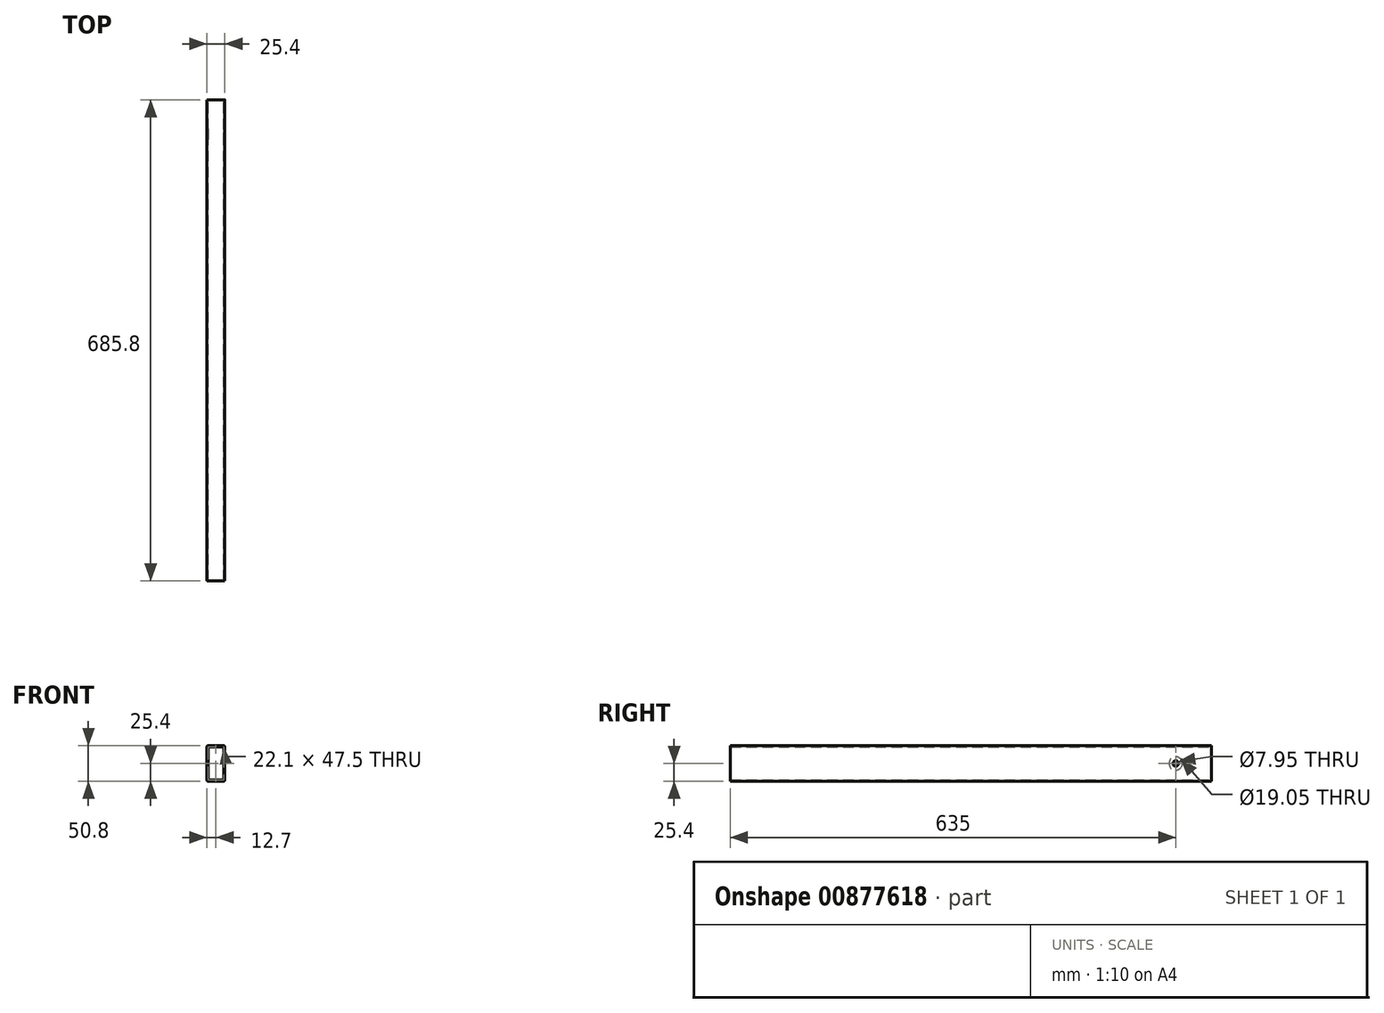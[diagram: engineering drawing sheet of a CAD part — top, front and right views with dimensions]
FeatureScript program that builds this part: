
annotation { "Feature Type Name" : "Feature", "Feature Type Description" : "" }
export const myFeature = defineFeature(function(context is Context, id is Id, definition is map)
    precondition{}
    {
        {
            var Q0;
            Q0=qCreatedBy(makeId("Front.planeOp"),FACE);
            var sketch = newSketch(context, id + "F0", { "sketchPlane" : qUnion([Q0])});
            skLineSegment(sketch, "E0.bottom", {"start": v(1.65, 0) * mm, "end": v(23.75, 0) * mm});
            skLineSegment(sketch, "E0.top", {"start": v(1.65, 50.8) * mm, "end": v(23.75, 50.8) * mm});
            skLineSegment(sketch, "E0.left", {"start": v(0, 1.65) * mm, "end": v(0, 49.15) * mm});
            skLineSegment(sketch, "E0.right", {"start": v(25.4, 1.65) * mm, "end": v(25.4, 49.15) * mm});
            skPoint(sketch, "E1.visualSharp", {"position": v(0, 50.8) * mm});
            skArc(sketch, "E1.filletArc", {"start": v(1.65, 50.8) * mm, "mid": v(0.48, 50.32) * mm, "end": v(0, 49.15) * mm});
            skPoint(sketch, "E2.visualSharp", {"position": v(25.4, 50.8) * mm});
            skArc(sketch, "E2.filletArc", {"start": v(25.4, 49.15) * mm, "mid": v(24.92, 50.32) * mm, "end": v(23.75, 50.8) * mm});
            skPoint(sketch, "E3.visualSharp", {"position": v(25.4, 0) * mm});
            skArc(sketch, "E3.filletArc", {"start": v(23.75, 0) * mm, "mid": v(24.92, 0.48) * mm, "end": v(25.4, 1.65) * mm});
            skPoint(sketch, "E4.visualSharp", {"position": v(0, 0) * mm});
            skArc(sketch, "E4.filletArc", {"start": v(0, 1.65) * mm, "mid": v(0.48, 0.48) * mm, "end": v(1.65, 0) * mm});
            skLineSegment(sketch, "E5.0", {"start": v(23.75, 1.65) * mm, "end": v(23.75, 49.15) * mm});
            skLineSegment(sketch, "E5.1", {"start": v(1.65, 1.65) * mm, "end": v(23.75, 1.65) * mm});
            skLineSegment(sketch, "E5.2", {"start": v(1.65, 1.65) * mm, "end": v(1.65, 49.15) * mm});
            skLineSegment(sketch, "E5.3", {"start": v(1.65, 49.15) * mm, "end": v(23.75, 49.15) * mm});
            skSolve(sketch);
        }
        {
            var Q0;
            Q0=qSketchRegion(id+"F0",true);
            extrude(context, id + "F1", {"entities" : qUnion([Q0]), "depth" : 685.8 * mm, "offsetDistance" : 25.4 * mm});
        }
        {
            var Q0;
            Q0=makeQuery(id+"F1.opExtrude","SWEPT_FACE",FACE,{"disambiguationData":[OSD([sQuery(id+"F0.wireOp",EDGE,"E0.right")])]});
            var sketch = newSketch(context, id + "F2", { "sketchPlane" : qUnion([Q0])});
            skCircle(sketch, "E6", {"center": v(-50.8, 25.4) * mm, "radius": 3.98 * mm});
            skPoint(sketch, "E6.centerSnap0", {"position": v(0, 25.4) * mm});
            skSolve(sketch);
        }
        {
            var Q0;
            Q0=qSketchRegion(id+"F2",true);
            extrude(context, id + "F3", {"entities" : qUnion([Q0]), "operationType" : NewBodyOperationType.REMOVE, "endBound" : BoundingType.UP_TO_NEXT, "oppositeDirection" : true, "depth" : 25.4 * mm, "offsetDistance" : 25.4 * mm});
        }
        {
            var Q0;
            Q0=makeQuery(id+"F1.opExtrude","SWEPT_FACE",FACE,{"disambiguationData":[OSD([sQuery(id+"F0.wireOp",EDGE,"E0.left")])]});
            var sketch = newSketch(context, id + "F4", { "sketchPlane" : qUnion([Q0])});
            skCircle(sketch, "E7", {"center": v(50.8, 25.4) * mm, "radius": 9.53 * mm});
            skPoint(sketch, "E7.centerSnap0", {"position": v(0, 25.4) * mm});
            skSolve(sketch);
        }
        {
            var Q0;
            Q0=qSketchRegion(id+"F4",true);
            extrude(context, id + "F5", {"entities" : qUnion([Q0]), "operationType" : NewBodyOperationType.REMOVE, "endBound" : BoundingType.UP_TO_NEXT, "oppositeDirection" : true, "depth" : 25.4 * mm, "offsetDistance" : 25.4 * mm});
        }
    });
